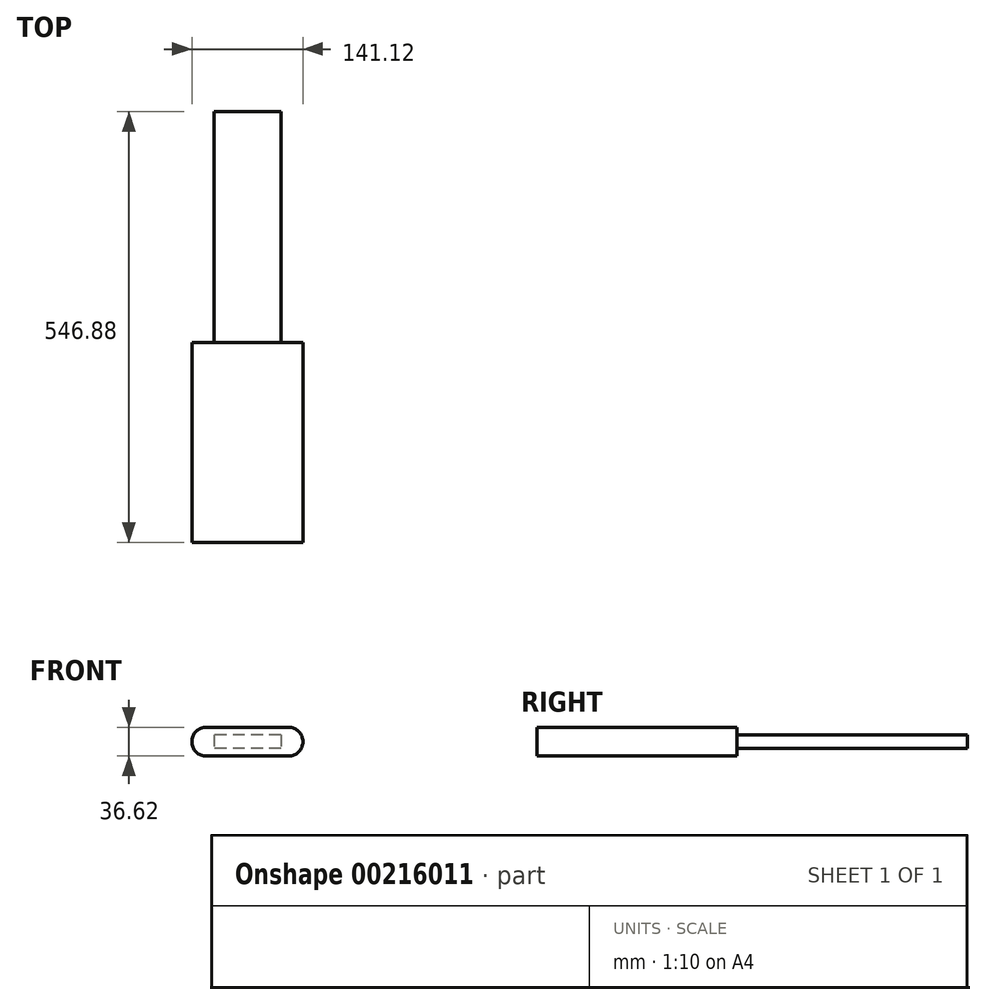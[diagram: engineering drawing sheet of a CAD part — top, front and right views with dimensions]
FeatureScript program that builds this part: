
annotation { "Feature Type Name" : "Feature", "Feature Type Description" : "" }
export const myFeature = defineFeature(function(context is Context, id is Id, definition is map)
    precondition{}
    {
        {
            var Q0;
            Q0=qCreatedBy(makeId("Front.planeOp"),FACE);
            var sketch = newSketch(context, id + "F0", { "sketchPlane" : qUnion([Q0])});
            skLineSegment(sketch, "E0.bottom", {"start": v(-52.24, 18.31) * mm, "end": v(52.24, 18.31) * mm});
            skLineSegment(sketch, "E0.top", {"start": v(-52.24, -18.31) * mm, "end": v(52.24, -18.31) * mm});
            skPoint(sketch, "E0.middle", {"position": v(0, 0) * mm});
            skArc(sketch, "E1", {"start": v(-52.24, 18.31) * mm, "mid": v(-70.56, 0) * mm, "end": v(-52.24, -18.31) * mm});
            skArc(sketch, "E2.MirrorC", {"start": v(52.24, 18.31) * mm, "mid": v(70.56, 0) * mm, "end": v(52.24, -18.31) * mm});
            skPoint(sketch, "E3.orphan", {"position": v(52.24, -18.31) * mm});
            skPoint(sketch, "E4.MirrorCS.start.orphan", {"position": v(52.24, 18.31) * mm});
            skPoint(sketch, "E5.orphan", {"position": v(0, -18.31) * mm});
            skPoint(sketch, "E6.start.orphan", {"position": v(0, 18.31) * mm});
            skSolve(sketch);
        }
        {
            var Q0;
            Q0=makeQuery(id+"F0.imprint","IMPRINT",FACE,{"disambiguationData":[TD([[makeQuery(id+"F0.imprint","IMPRINT",EDGE,{"derivedFrom":sQuery(id+"F0.wireOp",EDGE,"E0.bottom")}),-1.0]])]});
            extrude(context, id + "F1", {"entities" : qUnion([Q0]), "depth" : 254 * mm});
        }
        {
            var Q0;
            Q0=qCreatedBy(makeId("Front.planeOp"),FACE);
            var sketch = newSketch(context, id + "F2", { "sketchPlane" : qUnion([Q0])});
            skLineSegment(sketch, "E7.bottom", {"start": v(42.57, 8.76) * mm, "end": v(-42.57, 8.76) * mm});
            skLineSegment(sketch, "E7.top", {"start": v(42.57, -8.76) * mm, "end": v(-42.57, -8.76) * mm});
            skLineSegment(sketch, "E7.left", {"start": v(42.57, 8.76) * mm, "end": v(42.57, -8.76) * mm});
            skLineSegment(sketch, "E7.right", {"start": v(-42.57, 8.76) * mm, "end": v(-42.57, -8.76) * mm});
            skPoint(sketch, "E7.middle", {"position": v(0, 0) * mm});
            skSolve(sketch);
        }
        {
            var Q0;
            Q0=makeQuery(id+"F2.imprint","IMPRINT",FACE,{"disambiguationData":[TD([[makeQuery(id+"F2.imprint","IMPRINT",EDGE,{"derivedFrom":sQuery(id+"F2.wireOp",EDGE,"E7.bottom")}),1.0]])]});
            extrude(context, id + "F3", {"entities" : qUnion([Q0]), "operationType" : NewBodyOperationType.ADD, "endBound" : BoundingType.THROUGH_ALL, "oppositeDirection" : true, "depth" : 38.1 * mm});
        }
    });
